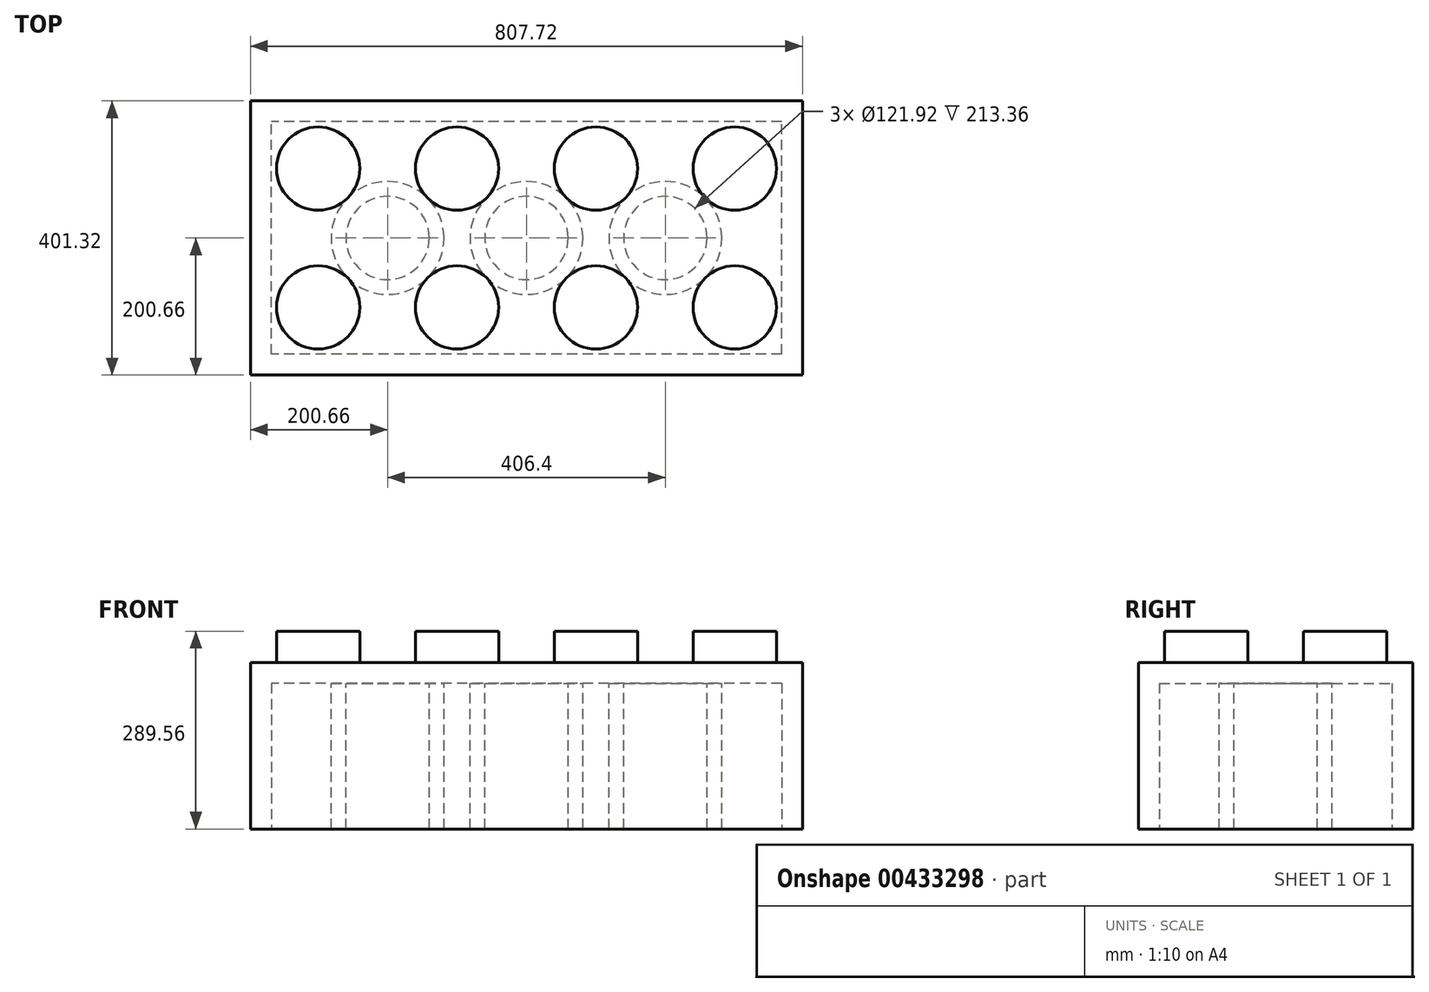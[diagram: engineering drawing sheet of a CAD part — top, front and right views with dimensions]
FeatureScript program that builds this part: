
annotation { "Feature Type Name" : "Feature", "Feature Type Description" : "" }
export const myFeature = defineFeature(function(context is Context, id is Id, definition is map)
    precondition{}
    {
        {
            var Q0;
            Q0=qCreatedBy(makeId("Top.planeOp"),FACE);
            var sketch = newSketch(context, id + "F0", { "sketchPlane" : qUnion([Q0])});
            skLineSegment(sketch, "E0.bottom", {"start": v(-403.86, -200.66) * mm, "end": v(403.86, -200.66) * mm});
            skLineSegment(sketch, "E0.top", {"start": v(-403.86, 200.66) * mm, "end": v(403.86, 200.66) * mm});
            skLineSegment(sketch, "E0.left", {"start": v(-403.86, -200.66) * mm, "end": v(-403.86, 200.66) * mm});
            skLineSegment(sketch, "E0.right", {"start": v(403.86, -200.66) * mm, "end": v(403.86, 200.66) * mm});
            skPoint(sketch, "E0.middle", {"position": v(0, 0) * mm});
            skSolve(sketch);
        }
        {
            var Q0;
            Q0=qCreatedBy(makeId("Top.planeOp"),FACE);
            var sketch = newSketch(context, id + "F1", { "sketchPlane" : qUnion([Q0])});
            skCircle(sketch, "E1", {"center": v(-304.8, 101.6) * mm, "radius": 60.96 * mm});
            skCircle(sketch, "E2.0.1.0", {"center": v(-304.8, -101.6) * mm, "radius": 60.96 * mm});
            skCircle(sketch, "E2.1.0.0", {"center": v(-101.6, 101.6) * mm, "radius": 60.96 * mm});
            skCircle(sketch, "E2.1.1.0", {"center": v(-101.6, -101.6) * mm, "radius": 60.96 * mm});
            skCircle(sketch, "E2.2.0.0", {"center": v(101.6, 101.6) * mm, "radius": 60.96 * mm});
            skCircle(sketch, "E2.2.1.0", {"center": v(101.6, -101.6) * mm, "radius": 60.96 * mm});
            skCircle(sketch, "E2.3.0.0", {"center": v(304.8, 101.6) * mm, "radius": 60.96 * mm});
            skCircle(sketch, "E2.3.1.0", {"center": v(304.8, -101.6) * mm, "radius": 60.96 * mm});
            skLineSegment(sketch, "E2.direction1", {"start": v(-304.8, 101.6) * mm, "end": v(-101.6, 101.6) * mm, "construction": true});
            skLineSegment(sketch, "E2.direction2", {"start": v(-304.8, 101.6) * mm, "end": v(-304.8, -101.6) * mm, "construction": true});
            skSolve(sketch);
        }
        {
            var Q0;
            Q0=makeQuery(id+"F0.imprint","IMPRINT",FACE,{"disambiguationData":[TD([[makeQuery(id+"F0.imprint","IMPRINT",EDGE,{"derivedFrom":sQuery(id+"F0.wireOp",EDGE,"E0.bottom")}),1.0]])]});
            extrude(context, id + "F2", {"entities" : qUnion([Q0]), "oppositeDirection" : true, "depth" : 243.84 * mm});
        }
        {
            var Q0;
            Q0=makeQuery(id+"F1.imprint","IMPRINT",FACE,{"disambiguationData":[TD([[makeQuery(id+"F1.imprint","IMPRINT",EDGE,{"derivedFrom":sQuery(id+"F1.wireOp",EDGE,"E1")}),1.0]])]});
            var Q1;
            Q1=makeQuery(id+"F1.imprint","IMPRINT",FACE,{"disambiguationData":[TD([[makeQuery(id+"F1.imprint","IMPRINT",EDGE,{"derivedFrom":sQuery(id+"F1.wireOp",EDGE,"E2.1.0.0")}),1.0]])]});
            var Q2;
            Q2=makeQuery(id+"F1.imprint","IMPRINT",FACE,{"disambiguationData":[TD([[makeQuery(id+"F1.imprint","IMPRINT",EDGE,{"derivedFrom":sQuery(id+"F1.wireOp",EDGE,"E2.2.0.0")}),1.0]])]});
            var Q3;
            Q3=makeQuery(id+"F1.imprint","IMPRINT",FACE,{"disambiguationData":[TD([[makeQuery(id+"F1.imprint","IMPRINT",EDGE,{"derivedFrom":sQuery(id+"F1.wireOp",EDGE,"E2.3.0.0")}),1.0]])]});
            var Q4;
            Q4=makeQuery(id+"F1.imprint","IMPRINT",FACE,{"disambiguationData":[TD([[makeQuery(id+"F1.imprint","IMPRINT",EDGE,{"derivedFrom":sQuery(id+"F1.wireOp",EDGE,"E2.3.1.0")}),1.0]])]});
            var Q5;
            Q5=makeQuery(id+"F1.imprint","IMPRINT",FACE,{"disambiguationData":[TD([[makeQuery(id+"F1.imprint","IMPRINT",EDGE,{"derivedFrom":sQuery(id+"F1.wireOp",EDGE,"E2.2.1.0")}),1.0]])]});
            var Q6;
            Q6=makeQuery(id+"F1.imprint","IMPRINT",FACE,{"disambiguationData":[TD([[makeQuery(id+"F1.imprint","IMPRINT",EDGE,{"derivedFrom":sQuery(id+"F1.wireOp",EDGE,"E2.1.1.0")}),1.0]])]});
            var Q7;
            Q7=makeQuery(id+"F1.imprint","IMPRINT",FACE,{"disambiguationData":[TD([[makeQuery(id+"F1.imprint","IMPRINT",EDGE,{"derivedFrom":sQuery(id+"F1.wireOp",EDGE,"E2.0.1.0")}),1.0]])]});
            extrude(context, id + "F3", {"entities" : qUnion([Q0, Q1, Q2, Q3, Q4, Q5, Q6, Q7]), "operationType" : NewBodyOperationType.ADD, "depth" : 45.72 * mm});
        }
        {
            var Q0;
            Q0=makeQuery(id+"F2.opExtrude","CAP_FACE",FACE,{"disambiguationData":[OSD([sQuery(id+"F0.wireOp",EDGE,"E0.bottom"),sQuery(id+"F0.wireOp",EDGE,"E0.top"),sQuery(id+"F0.wireOp",EDGE,"E0.left"),sQuery(id+"F0.wireOp",EDGE,"E0.right")])],"isStart":false});
            var sketch = newSketch(context, id + "F4", { "sketchPlane" : qUnion([Q0])});
            skLineSegment(sketch, "E3.bottom", {"start": v(373.38, 170.18) * mm, "end": v(-373.38, 170.18) * mm});
            skLineSegment(sketch, "E3.top", {"start": v(373.38, -170.18) * mm, "end": v(-373.38, -170.18) * mm});
            skLineSegment(sketch, "E3.left", {"start": v(373.38, 170.18) * mm, "end": v(373.38, -170.18) * mm});
            skLineSegment(sketch, "E3.right", {"start": v(-373.38, 170.18) * mm, "end": v(-373.38, -170.18) * mm});
            skPoint(sketch, "E3.middle", {"position": v(0, 0) * mm});
            skSolve(sketch);
        }
        {
            var Q0;
            Q0=makeQuery(id+"F4.imprint","IMPRINT",FACE,{"disambiguationData":[TD([[makeQuery(id+"F4.imprint","IMPRINT",EDGE,{"derivedFrom":sQuery(id+"F4.wireOp",EDGE,"E3.bottom")}),1.0]])]});
            extrude(context, id + "F5", {"entities" : qUnion([Q0]), "operationType" : NewBodyOperationType.REMOVE, "oppositeDirection" : true, "depth" : 213.36 * mm});
        }
        {
            var Q0;
            Q0=makeQuery(id+"F5.boolean.opBoolean","COPY",FACE,{"derivedFrom":makeQuery(id+"F5.opExtrude","CAP_FACE",FACE,{"disambiguationData":[OSD([sQuery(id+"F4.wireOp",EDGE,"E3.bottom"),sQuery(id+"F4.wireOp",EDGE,"E3.top"),sQuery(id+"F4.wireOp",EDGE,"E3.left"),sQuery(id+"F4.wireOp",EDGE,"E3.right")])],"isStart":false})});
            var sketch = newSketch(context, id + "F6", { "sketchPlane" : qUnion([Q0])});
            skCircle(sketch, "E4", {"center": v(-203.2, 0) * mm, "radius": 60.96 * mm});
            skCircle(sketch, "E5", {"center": v(-203.2, 0) * mm, "radius": 82.55 * mm});
            skCircle(sketch, "E6.1.0.0", {"center": v(0, 0) * mm, "radius": 60.96 * mm});
            skCircle(sketch, "E6.1.0.1", {"center": v(0, 0) * mm, "radius": 82.55 * mm});
            skCircle(sketch, "E6.2.0.0", {"center": v(203.2, 0) * mm, "radius": 60.96 * mm});
            skCircle(sketch, "E6.2.0.1", {"center": v(203.2, 0) * mm, "radius": 82.55 * mm});
            skLineSegment(sketch, "E6.direction1", {"start": v(-203.2, 0) * mm, "end": v(0, 0) * mm, "construction": true});
            skSolve(sketch);
        }
        {
            var Q0;
            Q0=makeQuery(id+"F6.imprint","IMPRINT",FACE,{"disambiguationData":[TD([[makeQuery(id+"F6.imprint","IMPRINT",EDGE,{"derivedFrom":sQuery(id+"F6.wireOp",EDGE,"E4")}),-1.0]])]});
            var Q1;
            Q1=makeQuery(id+"F6.imprint","IMPRINT",FACE,{"disambiguationData":[TD([[makeQuery(id+"F6.imprint","IMPRINT",EDGE,{"derivedFrom":sQuery(id+"F6.wireOp",EDGE,"E6.1.0.0")}),-1.0]])]});
            var Q2;
            Q2=makeQuery(id+"F6.imprint","IMPRINT",FACE,{"disambiguationData":[TD([[makeQuery(id+"F6.imprint","IMPRINT",EDGE,{"derivedFrom":sQuery(id+"F6.wireOp",EDGE,"E6.2.0.0")}),-1.0]])]});
            extrude(context, id + "F7", {"entities" : qUnion([Q0, Q1, Q2]), "operationType" : NewBodyOperationType.ADD, "depth" : 213.36 * mm});
        }
    });
